# Revit family: V_DP-RC_125_2024_eng
name_source: partatom
category: Mechanical Equipment
units: mm (PartAtom-declared; Revit-internal decimal feet)

## family parameters
Always vertical = Yes
Cut with Voids When Loaded = No
Maintain Annotation Orientation = No
OmniClass Number = 23.75.00.00
OmniClass Title = Climate Control (HVAC)
Part Type = Normal
Room Calculation Point = No
Round Connector Dimension = Use Diameter
Shared = No
Work Plane-Based = No

## types (1)
- 125mm Ceiling Integrated Valve
    Amperage = 0 A
    B = 80 mm  [stored 0.262467 ft]
    Casing Material = ABS (white)
    D = 124 mm  [stored 0.406824 ft]
    D1 = 250 mm  [stored 0.82021 ft]
    D2 = 234 mm  [stored 0.767717 ft]
    Default Elevation = 0 mm  [stored 0 ft]
    Frequency = 0 Hz
    H = 99 mm  [stored 0.324803 ft]
    H1 = 50 mm  [stored 0.164042 ft]
    L = 323 mm  [stored 1.05971 ft]
    Manufacturer = Airflow Developments
    Material metal = galvanized steel
    Maximum Air Flow = 90.0 m³/h
    Number of Fase = 1
    Part number = 90002245
    Power = 0 W
    Product name = 125mm Round Ceiling Integrated Air Valve
    Voltage = 0 V
    Weight = 4.50 kg

note: [stored X ft] marks values corroborated as IEEE doubles in the binary element streams (Revit-internal decimal feet)

## geometry (parser evidence)
native form markers: Sweep x16
no freeform markers — native parametric forms only
